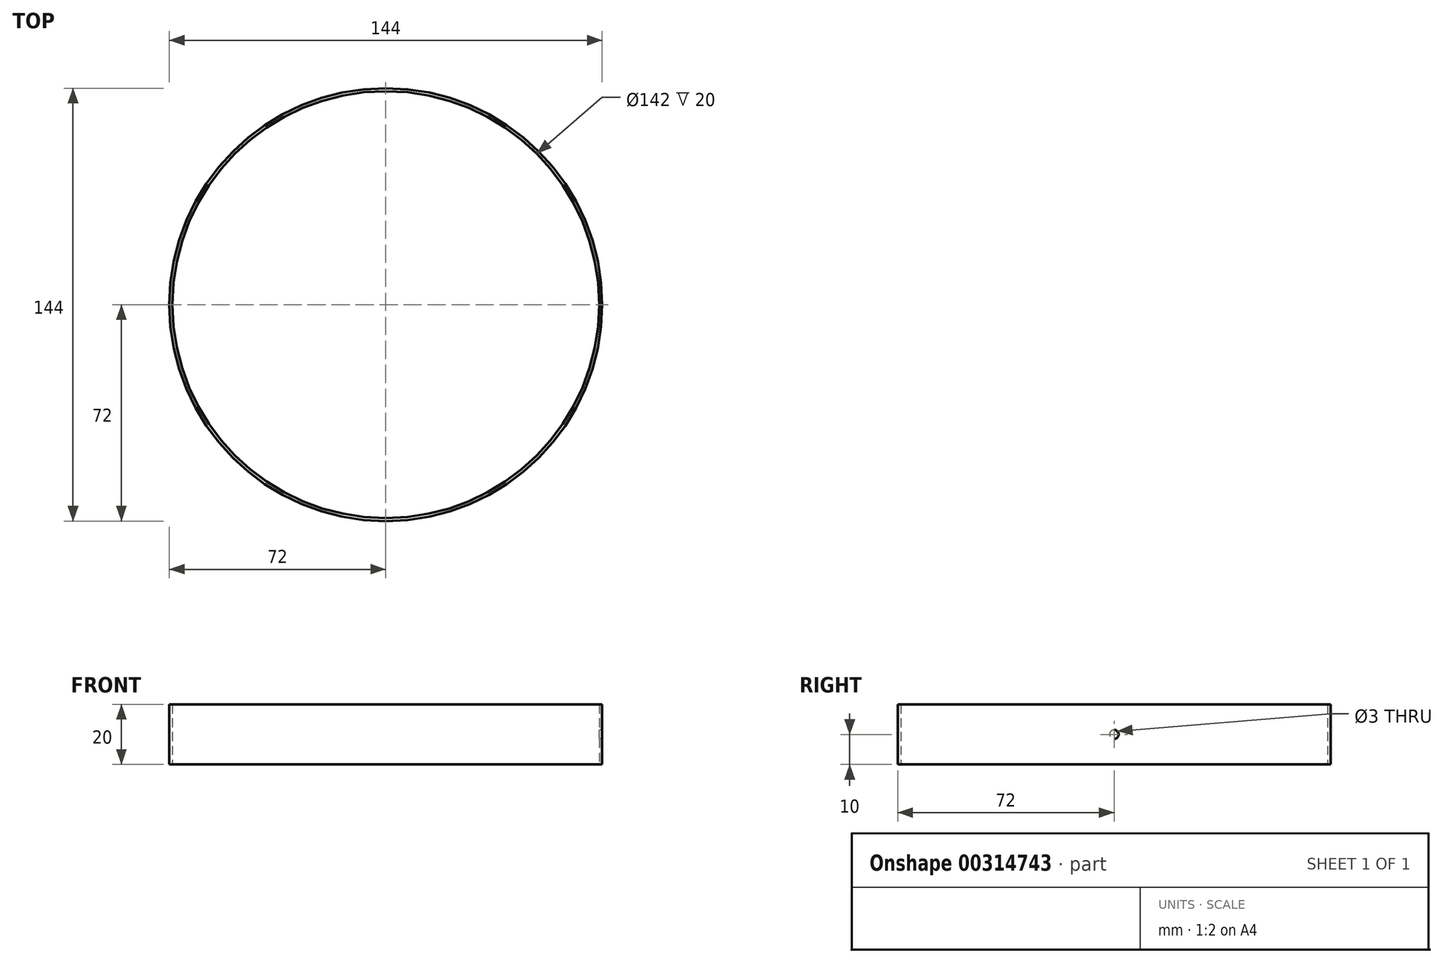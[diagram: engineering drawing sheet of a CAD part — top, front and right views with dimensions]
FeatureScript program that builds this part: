
annotation { "Feature Type Name" : "Feature", "Feature Type Description" : "" }
export const myFeature = defineFeature(function(context is Context, id is Id, definition is map)
    precondition{}
    {
        {
            var Q0;
            Q0=qCreatedBy(makeId("Top.planeOp"),FACE);
            var sketch = newSketch(context, id + "F0", { "sketchPlane" : qUnion([Q0])});
            skCircle(sketch, "E0", {"center": v(0, 0) * mm, "radius": 75 * mm});
            skCircle(sketch, "E1.0", {"center": v(0, 0) * mm, "radius": 74 * mm});
            skCircle(sketch, "E2.0", {"center": v(0, 0) * mm, "radius": 72 * mm});
            skCircle(sketch, "E3.0", {"center": v(0, 0) * mm, "radius": 71 * mm});
            skCircle(sketch, "E4.0", {"center": v(0, 0) * mm, "radius": 69 * mm});
            skCircle(sketch, "E5.0", {"center": v(0, 0) * mm, "radius": 68 * mm});
            skCircle(sketch, "E6.0", {"center": v(0, 0) * mm, "radius": 66 * mm});
            skCircle(sketch, "E7.0", {"center": v(0, 0) * mm, "radius": 65 * mm});
            skCircle(sketch, "E8.0", {"center": v(0, 0) * mm, "radius": 63 * mm});
            skCircle(sketch, "E9.0", {"center": v(0, 0) * mm, "radius": 62 * mm});
            skCircle(sketch, "E10.0", {"center": v(0, 0) * mm, "radius": 60 * mm});
            skCircle(sketch, "E11.0", {"center": v(0, 0) * mm, "radius": 59 * mm});
            skCircle(sketch, "E12.0", {"center": v(0, 0) * mm, "radius": 57 * mm});
            skCircle(sketch, "E13.0", {"center": v(0, 0) * mm, "radius": 56.05 * mm});
            skCircle(sketch, "E14.0", {"center": v(0, 0) * mm, "radius": 54.05 * mm});
            skCircle(sketch, "E15.0", {"center": v(0, 0) * mm, "radius": 53.05 * mm});
            skSolve(sketch);
        }
        {
            var Q0;
            Q0=makeQuery(id+"F0.imprint","IMPRINT",FACE,{"disambiguationData":[TD([[makeQuery(id+"F0.imprint","IMPRINT",EDGE,{"derivedFrom":sQuery(id+"F0.wireOp",EDGE,"E2.0")}),1.0]])]});
            extrude(context, id + "F1", {"entities" : qUnion([Q0]), "depth" : 20 * mm});
        }
        {
            var Q0;
            Q0=qCreatedBy(makeId("Right.planeOp"),FACE);
            var sketch = newSketch(context, id + "F2", { "sketchPlane" : qUnion([Q0])});
            skCircle(sketch, "E16", {"center": v(0, 10) * mm, "radius": 1.5 * mm});
            skSolve(sketch);
        }
        {
            var Q0;
            Q0=qSketchRegion(id+"F2",true);
            extrude(context, id + "F3", {"entities" : qUnion([Q0]), "operationType" : NewBodyOperationType.REMOVE, "depth" : 86.5 * mm});
        }
    });
